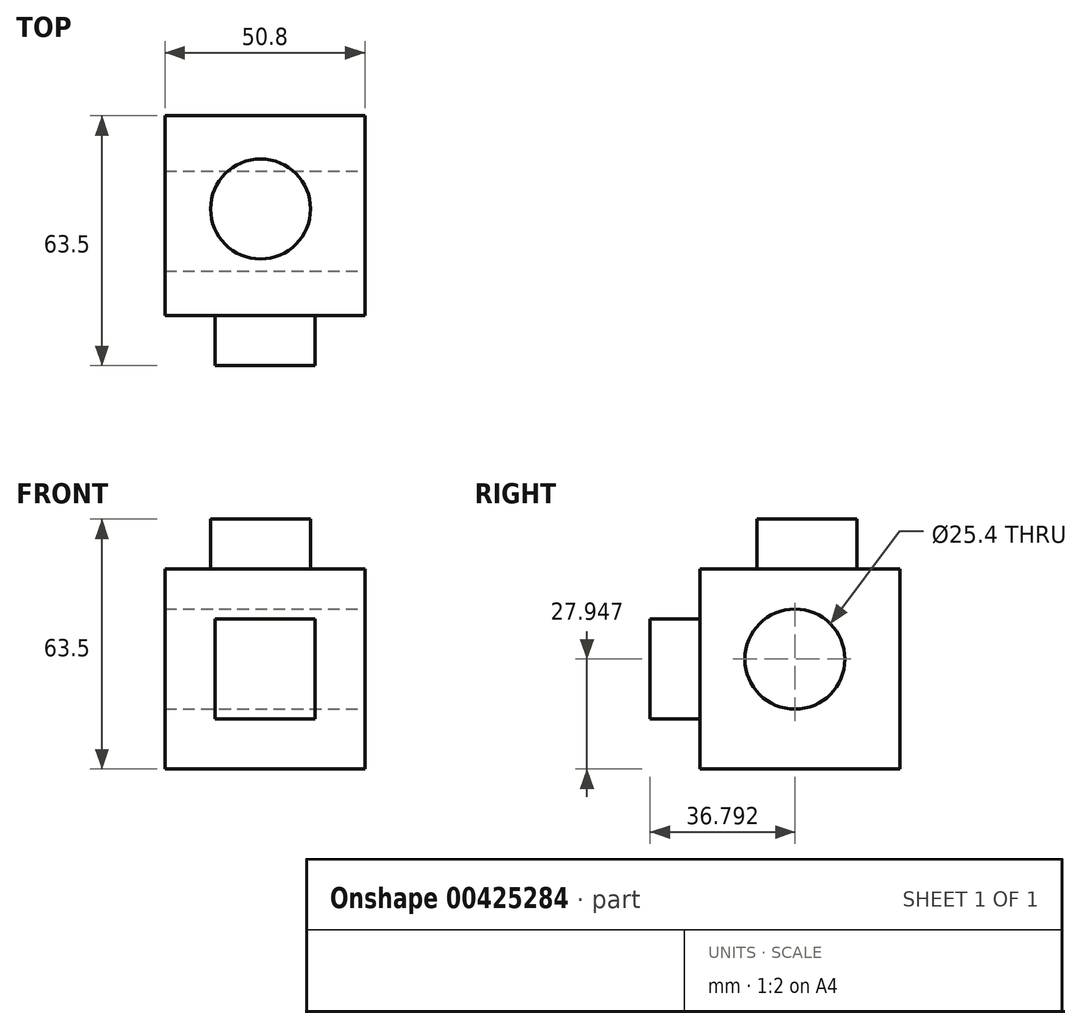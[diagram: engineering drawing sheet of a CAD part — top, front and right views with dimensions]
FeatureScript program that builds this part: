
annotation { "Feature Type Name" : "Feature", "Feature Type Description" : "" }
export const myFeature = defineFeature(function(context is Context, id is Id, definition is map)
    precondition{}
    {
        {
            var Q0;
            Q0=qCreatedBy(makeId("Front.planeOp"),FACE);
            var sketch = newSketch(context, id + "F0", { "sketchPlane" : qUnion([Q0])});
            skLineSegment(sketch, "E0.bottom", {"start": v(0, 0) * mm, "end": v(-50.8, 0) * mm});
            skLineSegment(sketch, "E0.top", {"start": v(0, 50.8) * mm, "end": v(-50.8, 50.8) * mm});
            skLineSegment(sketch, "E0.left", {"start": v(0, 0) * mm, "end": v(0, 50.8) * mm});
            skLineSegment(sketch, "E0.right", {"start": v(-50.8, 0) * mm, "end": v(-50.8, 50.8) * mm});
            skSolve(sketch);
        }
        {
            var Q0;
            Q0=makeQuery(id+"F0.imprint","IMPRINT",FACE,{"disambiguationData":[TD([[makeQuery(id+"F0.imprint","IMPRINT",EDGE,{"derivedFrom":sQuery(id+"F0.wireOp",EDGE,"E0.bottom")}),-1.0]])]});
            extrude(context, id + "F1", {"entities" : qUnion([Q0]), "depth" : 50.8 * mm});
        }
        {
            var Q0;
            Q0=makeQuery(id+"F1.opExtrude","SWEPT_FACE",FACE,{"disambiguationData":[OSD([sQuery(id+"F0.wireOp",EDGE,"E0.left")])]});
            var sketch = newSketch(context, id + "F2", { "sketchPlane" : qUnion([Q0])});
            skCircle(sketch, "E1", {"center": v(-26.7, 27.95) * mm, "radius": 12.7 * mm});
            skSolve(sketch);
        }
        {
            var Q0;
            Q0=makeQuery(id+"F2.imprint","IMPRINT",FACE,{"disambiguationData":[TD([[makeQuery(id+"F2.imprint","IMPRINT",EDGE,{"derivedFrom":sQuery(id+"F2.wireOp",EDGE,"E1")}),1.0]])]});
            extrude(context, id + "F3", {"entities" : qUnion([Q0]), "operationType" : NewBodyOperationType.REMOVE, "oppositeDirection" : true, "depth" : 53.34 * mm});
        }
        {
            var Q0;
            Q0=makeQuery(id+"F1.opExtrude","CAP_FACE",FACE,{"disambiguationData":[OSD([sQuery(id+"F0.wireOp",EDGE,"E0.bottom"),sQuery(id+"F0.wireOp",EDGE,"E0.top"),sQuery(id+"F0.wireOp",EDGE,"E0.left"),sQuery(id+"F0.wireOp",EDGE,"E0.right")])],"isStart":false});
            var sketch = newSketch(context, id + "F4", { "sketchPlane" : qUnion([Q0])});
            skLineSegment(sketch, "E2.bottom", {"start": v(-12.7, 12.7) * mm, "end": v(-38.1, 12.7) * mm});
            skLineSegment(sketch, "E2.top", {"start": v(-12.7, 38.1) * mm, "end": v(-38.1, 38.1) * mm});
            skLineSegment(sketch, "E2.left", {"start": v(-12.7, 12.7) * mm, "end": v(-12.7, 38.1) * mm});
            skLineSegment(sketch, "E2.right", {"start": v(-38.1, 12.7) * mm, "end": v(-38.1, 38.1) * mm});
            skSolve(sketch);
        }
        {
            var Q0;
            Q0=makeQuery(id+"F4.imprint","IMPRINT",FACE,{"disambiguationData":[TD([[makeQuery(id+"F4.imprint","IMPRINT",EDGE,{"derivedFrom":sQuery(id+"F4.wireOp",EDGE,"E2.bottom")}),-1.0]])]});
            extrude(context, id + "F5", {"entities" : qUnion([Q0]), "operationType" : NewBodyOperationType.ADD, "depth" : 12.7 * mm});
        }
        {
            var Q0;
            Q0=makeQuery(id+"F1.opExtrude","SWEPT_FACE",FACE,{"disambiguationData":[OSD([sQuery(id+"F0.wireOp",EDGE,"E0.top")])]});
            var sketch = newSketch(context, id + "F6", { "sketchPlane" : qUnion([Q0])});
            skCircle(sketch, "E3", {"center": v(-26.48, -23.66) * mm, "radius": 12.7 * mm});
            skSolve(sketch);
        }
        {
            var Q0;
            Q0 = qSketchRegion(id + "F6", true);
            extrude(context, id + "F7", {"entities" : qUnion([Q0]), "operationType" : NewBodyOperationType.ADD, "depth" : 12.7 * mm});
        }
    });
